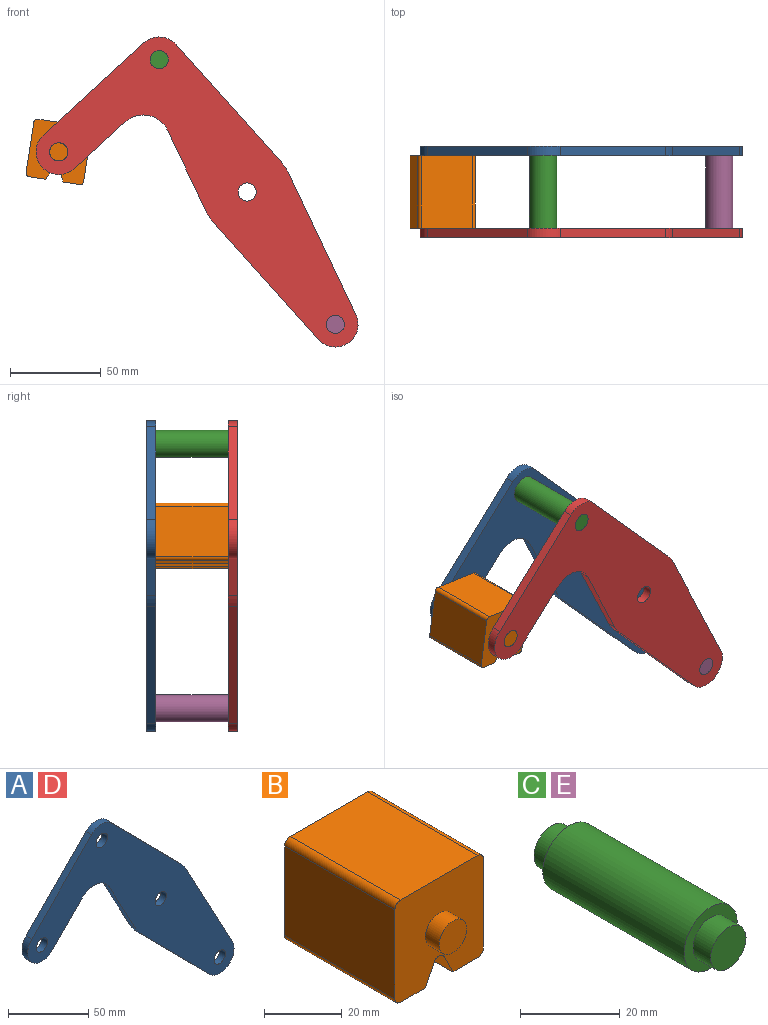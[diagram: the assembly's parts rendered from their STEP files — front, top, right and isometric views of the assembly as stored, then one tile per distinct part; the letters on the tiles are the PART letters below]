
ASSEMBLY  parts=5 mates=3
PART A: 18 faces, bbox 181.7x5x165.8 mm
  f0: plane 43.49x23.35mm, normal (-0.88,0,-0.47), area 246.8mm2, adj f1,f14,f16,f17
  f1: cylinder r=25mm len=5.75mm, axis (0,1,0), area 35.8mm2, adj f0,f2,f16,f17
  f2: plane 61.6x60.87mm, normal (-0.71,0,-0.7), area 433mm2, adj f1,f3,f16,f17
  f3: cylinder r=12.5mm len=21.39mm, axis (0,1,0), area 178.4mm2, adj f2,f4,f16,f17
  f4: plane 76.3x40.96mm, normal (0.88,0,0.47), area 433mm2, adj f3,f5,f16,f17
  f5: cylinder r=25mm len=5.75mm, axis (0,1,0), area 35.8mm2, adj f4,f6,f16,f17
  f6: plane 61.6x60.87mm, normal (0.71,0,0.7), area 433mm2, adj f5,f7,f16,f17
  f7: cylinder r=12.5mm len=17.78mm, axis (0,1,0), area 98.9mm2, adj f6,f8,f16,f17
  f8: plane 53.35x52.71mm, normal (-0.71,0,0.7), area 375mm2, adj f7,f9,f16,f17
  f9: cylinder r=12.5mm len=21.39mm, axis (0,1,0), area 196.3mm2, adj f8,f10,f16,f17
  f10: plane 26.86x26.54mm, normal (0.71,0,-0.7), area 188.8mm2, adj f9,f14,f16,f17
  f11: cylinder r=5mm len=10mm, axis (0,1,0), area 157.1mm2, adj f16,f17
  f12: cylinder r=5mm len=10mm, axis (0,1,0), area 157.1mm2, adj f16,f17
  f13: cylinder r=5mm len=10mm, axis (0,1,0), area 157.1mm2, adj f16,f17
  f14: cylinder r=15mm len=23.89mm, axis (0,1,0), area 140.2mm2, adj f0,f10,f16,f17
  f15: cylinder r=5mm len=10mm, axis (0,1,0), area 157.1mm2, adj f16,f17
  f16: plane 181.66x165.78mm, normal (0,-1,0), area 8710.1mm2, adj f0,f1,f2,f3,f4,f5,f6,f7
  f17: plane 181.66x165.78mm, normal (0,1,0), area 8710.1mm2, adj f0,f1,f2,f3,f4,f5,f6,f7
PART B: 18 faces, bbox 32.1x50x32.1 mm
  f0: plane 40x28.08mm, normal (1,0,0), area 1123.1mm2, adj f4,f10,f13,f14
  f1: plane 40x9.04mm, normal (0,0,-1), area 361.6mm2, adj f2,f4,f10,f14
  f2: plane 40x6.42mm, normal (-0.89,0,-0.45), area 287.2mm2, adj f1,f4,f10,f15
  f3: plane 40x6.42mm, normal (0.89,0,-0.45), area 287.2mm2, adj f4,f5,f10,f15
  f4: plane 32.08x32.08mm, normal (0,-1,0), area 900.6mm2, adj f0,f1,f2,f3,f5,f6,f7,f9
  f5: plane 40x9.04mm, normal (0,0,-1), area 361.6mm2, adj f3,f4,f10,f16
  f6: plane 40x28.08mm, normal (0,0,1), area 1123.1mm2, adj f4,f10,f13,f17
  f7: plane 40x28.08mm, normal (-1,0,0), area 1123.1mm2, adj f4,f10,f16,f17
  f8: plane 10x10mm, normal (0,-1,0), area 78.5mm2, adj f9
  f9: cylinder r=5mm len=10mm, axis (0,1,0), area 157.1mm2, adj f4,f8
  f10: plane 32.08x32.08mm, normal (0,1,0), area 900.6mm2, adj f0,f1,f2,f3,f5,f6,f7,f12
  f11: plane 10x10mm, normal (0,1,0), area 78.5mm2, adj f12
  f12: cylinder r=5mm len=10mm, axis (0,-1,0), area 157.1mm2, adj f10,f11
  f13: cylinder r=2mm len=40mm, axis (0,1,0), area 125.7mm2, adj f0,f4,f6,f10
  f14: cylinder r=2mm len=40mm, axis (0,-1,0), area 125.7mm2, adj f0,f1,f4,f10
  f15: cylinder r=2mm len=40mm, axis (0,1,0), area 177.1mm2, adj f2,f3,f4,f10
  f16: cylinder r=2mm len=40mm, axis (0,1,0), area 125.7mm2, adj f4,f5,f7,f10
  f17: cylinder r=2mm len=40mm, axis (0,-1,0), area 125.7mm2, adj f4,f6,f7,f10
PART C: 7 faces, bbox 15x50x15 mm
  f0: cylinder r=7.5mm len=40mm, axis (0,-1,0), area 1885mm2, adj f2,f5
  f1: cylinder r=5mm len=10mm, axis (0,1,0), area 157.1mm2, adj f2,f3
  f2: plane 15x15mm, normal (0,-1,0), area 98.2mm2, adj f0,f1
  f3: plane 10x10mm, normal (0,-1,0), area 78.5mm2, adj f1
  f4: cylinder r=5mm len=10mm, axis (0,-1,0), area 157.1mm2, adj f5,f6
  f5: plane 15x15mm, normal (0,1,0), area 98.2mm2, adj f0,f4
  f6: plane 10x10mm, normal (0,1,0), area 78.5mm2, adj f4
PART D: same geometry as A
PART E: same geometry as C
PLACE A rot(axis=(0,1,0),2.8deg) t=(0,25,0)mm
PLACE B rot(axis=(0,1,0),8.8deg) t=(-2.88,-20,-10.72)mm
PLACE C rot(axis=(0,1,0),2.8deg) t=(0,-20,0)mm
PLACE D rot(axis=(0,1,0),2.8deg) t=(0,-20,0)mm fixed
PLACE E rot(axis=(0,1,0),2.8deg) t=(97,-20,-145.66)mm
MATE revolute B.f9 <-> D.f9  axis (0,-1,0) through (-103.74,-25,22.1)mm
MATE fastened E.f0 <-> D.f3  axis (0,-1,0) through (48.5,-20,-72.83)mm
MATE fastened A.f7 <-> C.f0  axis (0,1,0) through (-48.5,25,72.83)mm
